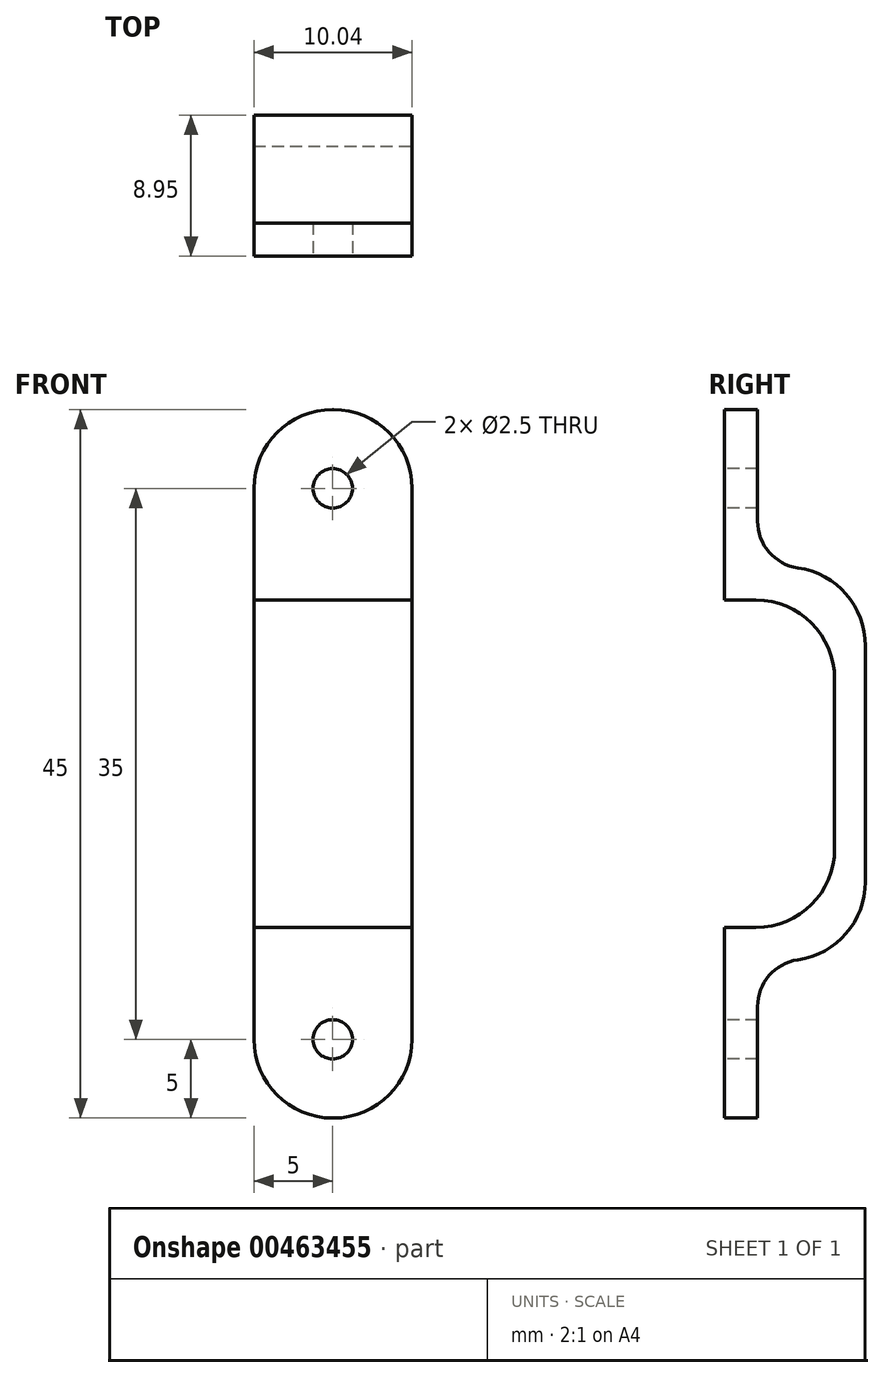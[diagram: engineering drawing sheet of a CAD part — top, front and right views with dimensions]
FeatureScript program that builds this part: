
annotation { "Feature Type Name" : "Feature", "Feature Type Description" : "" }
export const myFeature = defineFeature(function(context is Context, id is Id, definition is map)
    precondition{}
    {
        {
            var Q0;
            Q0=qCreatedBy(makeId("Top.planeOp"),FACE);
            var sketch = newSketch(context, id + "F0", { "sketchPlane" : qUnion([Q0])});
            skLineSegment(sketch, "E0", {"start": v(9.1, 2.1) * mm, "end": v(9.1, 0) * mm});
            skLineSegment(sketch, "E1", {"start": v(9.1, 2.1) * mm, "end": v(9.1, 8.95) * mm});
            skLineSegment(sketch, "E2", {"start": v(9.1, 8.95) * mm, "end": v(19.14, 8.95) * mm});
            skLineSegment(sketch, "E3", {"start": v(19.14, 8.95) * mm, "end": v(19.14, 0) * mm});
            skLineSegment(sketch, "E4", {"start": v(19.14, 0) * mm, "end": v(9.1, 0) * mm});
            skPoint(sketch, "E5.end.orphan", {"position": v(0, 0) * mm});
            skLineSegment(sketch, "E6", {"start": v(9.1, 2.1) * mm, "end": v(19.14, 2.1) * mm});
            skSolve(sketch);
        }
        {
            var Q0;
            Q0=qSketchRegion(id+"F0",true);
            extrude(context, id + "F1", {"entities" : qUnion([Q0]), "depth" : 25 * mm});
        }
        {
            var Q0;
            Q0=makeQuery(id+"F1.opExtrude","SWEPT_FACE",FACE,{"disambiguationData":[OSD([sQuery(id+"F0.wireOp",EDGE,"E3")])]});
            cPlane(context, id + "F2", {"entities" : qUnion([Q0]), "cplaneType" : CPlaneType.OFFSET, "offset" : 0 * mm, "width" : 150 * mm, "height" : 150 * mm});
        }
        {
            var Q0;
            Q0=makeQuery(id+"F0.imprint","IMPRINT",FACE,{"disambiguationData":[TD([[makeQuery(id+"F0.imprint","IMPRINT",EDGE,{"derivedFrom":sQuery(id+"F0.wireOp",EDGE,"E0")}),1.0]])]});
            extrude(context, id + "F3", {"entities" : qUnion([Q0]), "operationType" : NewBodyOperationType.ADD, "oppositeDirection" : true, "depth" : 10 * mm, "hasSecondDirection" : true, "secondDirectionOppositeDirection" : false, "secondDirectionDepth" : 35 * mm});
        }
        {
            var Q0;
            Q0=qCreatedBy(id+"F2.planeOp",FACE);
            var sketch = newSketch(context, id + "F4", { "sketchPlane" : qUnion([Q0])});
            skLineSegment(sketch, "E7", {"start": v(0, 0) * mm, "end": v(0, 2.1) * mm});
            skLineSegment(sketch, "E8", {"start": v(0, 2.1) * mm, "end": v(7, 2.1) * mm});
            skLineSegment(sketch, "E9", {"start": v(7, 2.1) * mm, "end": v(7, 22.9) * mm});
            skLineSegment(sketch, "E10", {"start": v(7, 22.9) * mm, "end": v(0, 22.9) * mm});
            skLineSegment(sketch, "E11", {"start": v(0, 22.9) * mm, "end": v(0, 2.1) * mm});
            skSolve(sketch);
        }
        {
            var Q0;
            Q0=qSketchRegion(id+"F4",true);
            extrude(context, id + "F5", {"entities" : qUnion([Q0]), "operationType" : NewBodyOperationType.REMOVE, "endBound" : BoundingType.THROUGH_ALL, "oppositeDirection" : true, "depth" : 10 * mm});
        }
        {
            var Q0;
            Q0=qCreatedBy(makeId("Front.planeOp"),FACE);
            var sketch = newSketch(context, id + "F6", { "sketchPlane" : qUnion([Q0])});
            skLineSegment(sketch, "E12", {"start": v(0, 0) * mm, "end": v(14.1, 0) * mm, "construction": true});
            skLineSegment(sketch, "E13", {"start": v(14.1, 0) * mm, "end": v(14.1, -5) * mm, "construction": true});
            skLineSegment(sketch, "E14", {"start": v(14.1, 0) * mm, "end": v(14.1, 30) * mm, "construction": true});
            skCircle(sketch, "E15", {"center": v(14.1, 30) * mm, "radius": 1.25 * mm});
            skCircle(sketch, "E16", {"center": v(14.1, -5) * mm, "radius": 1.25 * mm});
            skSolve(sketch);
        }
        {
            var Q0;
            Q0 = qSketchRegion(id + "F6", true);
            extrude(context, id + "F7", {"entities" : qUnion([Q0]), "operationType" : NewBodyOperationType.REMOVE, "oppositeDirection" : true, "depth" : 25 * mm});
        }
        {
            var Q0;
            Q0=makeQuery(id+"F3.opExtrude","CAP_EDGE",EDGE,{"disambiguationData":[OSD([sQuery(id+"F0.wireOp",EDGE,"E3")])],"isStart":true});
            var Q1;
            Q1=makeQuery(id+"F3.opExtrude","CAP_EDGE",EDGE,{"disambiguationData":[OSD([sQuery(id+"F0.wireOp",EDGE,"E0")])],"isStart":true});
            var Q2;
            Q2=makeQuery(id+"F3.opExtrude","CAP_EDGE",EDGE,{"disambiguationData":[OSD([sQuery(id+"F0.wireOp",EDGE,"E0")])],"isStart":false});
            var Q3;
            Q3=makeQuery(id+"F3.opExtrude","CAP_EDGE",EDGE,{"disambiguationData":[OSD([sQuery(id+"F0.wireOp",EDGE,"E3")])],"isStart":false});
            var Q4;
            Q4=makeQuery(id+"F5.boolean.opBoolean","COPY",EDGE,{"derivedFrom":makeQuery(id+"F5.opExtrude","SWEPT_EDGE",EDGE,{"disambiguationData":[OSD([sQuery(id+"F4.wireOp",EDGE,"E8"),sQuery(id+"F4.wireOp",EDGE,"E9")])]})});
            var Q5;
            Q5=makeQuery(id+"F5.boolean.opBoolean","COPY",EDGE,{"derivedFrom":makeQuery(id+"F5.opExtrude","SWEPT_EDGE",EDGE,{"disambiguationData":[OSD([sQuery(id+"F4.wireOp",EDGE,"E9"),sQuery(id+"F4.wireOp",EDGE,"E10")])]})});
            var Q6;
            Q6=makeQuery(id+"F1.opExtrude","CAP_EDGE",EDGE,{"disambiguationData":[OSD([sQuery(id+"F0.wireOp",EDGE,"E2")])],"isStart":true});
            var Q7;
            Q7=makeQuery(id+"F1.opExtrude","CAP_EDGE",EDGE,{"disambiguationData":[OSD([sQuery(id+"F0.wireOp",EDGE,"E2")])],"isStart":false});
            fillet(context, id + "F8", {"entities" : qUnion([Q0, Q1, Q2, Q3, Q4, Q5, Q6, Q7]), "radius" : 5 * mm, "tangentPropagation" : true, "allowEdgeOverflow" : false});
        }
        {
            var Q0;
            Q0=makeQuery(id+"F3.boolean.opBoolean","INTERSECT",EDGE,{"derivedFrom":[makeQuery(id+"F1.opExtrude","CAP_FACE",FACE,{"disambiguationData":[OSD([sQuery(id+"F0.wireOp",EDGE,"E0"),sQuery(id+"F0.wireOp",EDGE,"E1"),sQuery(id+"F0.wireOp",EDGE,"E2"),sQuery(id+"F0.wireOp",EDGE,"E3"),sQuery(id+"F0.wireOp",EDGE,"E4")])],"isStart":true}),makeQuery(id+"F3.opExtrude","SWEPT_FACE",FACE,{"disambiguationData":[OSD([sQuery(id+"F0.wireOp",EDGE,"E6")])]})]});
            var Q1;
            Q1=makeQuery(id+"F3.boolean.opBoolean","INTERSECT",EDGE,{"derivedFrom":[makeQuery(id+"F1.opExtrude","CAP_FACE",FACE,{"disambiguationData":[OSD([sQuery(id+"F0.wireOp",EDGE,"E0"),sQuery(id+"F0.wireOp",EDGE,"E1"),sQuery(id+"F0.wireOp",EDGE,"E2"),sQuery(id+"F0.wireOp",EDGE,"E3"),sQuery(id+"F0.wireOp",EDGE,"E4")])],"isStart":false}),makeQuery(id+"F3.opExtrude","SWEPT_FACE",FACE,{"disambiguationData":[OSD([sQuery(id+"F0.wireOp",EDGE,"E6")])]})]});
            fillet(context, id + "F9", {"entities" : qUnion([Q0, Q1]), "radius" : 3 * mm, "tangentPropagation" : true, "allowEdgeOverflow" : false});
        }
    });
